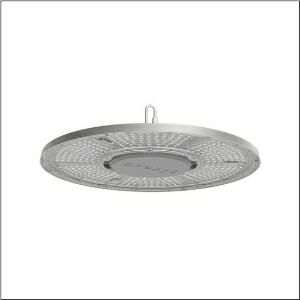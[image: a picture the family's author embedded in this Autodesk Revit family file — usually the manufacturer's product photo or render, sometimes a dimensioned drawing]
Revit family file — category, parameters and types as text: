
# Revit family: highbay_31-l_51hc42da4jmb
name_source: partatom
category: Lighting Fixtures
units: mm (PartAtom-declared; Revit-internal decimal feet)

## family parameters
Cut with Voids When Loaded = No
Host = Face
Light Source = No
Part Type = Normal
Room Calculation Point = No
Round Connector Dimension = Use Diameter
Shared = No

## types (1)
- Highbay 31-L (1 x LED, 20000 lm, 134 W, 4000K)
    Apparent Load = 134 VA
    CIE Flux Codes = 77 99 100 100 100
    Color Rendering = 80
    Color Temperature = 4000K
    Default Elevation = 1800 mm
    Description = Highbay 31-L, high bay luminaire, primary light control with lens, of PC, primary optical cover: cover panel, of PC, transparent, light emission: direct distribution, primary light characteristic: rotationally symmetric, installation type: suspended mounting, surface-mounted, LED, rated luminous flux: 20.000lm, luminous efficacy: 150lm/W, light colour: 840, colour temperature: 4000K, control gear: DALI 2, with cable, 5x 1.0mm², free wire ends, mains connection: 220..240V, AC/DC, 0/50..60Hz, cable length: 1,5m, rated input power: 134W, housing, rotationally symmetric, of diecast aluminium, powder-coated, grey aluminium (RAL 9007), with hook on luminaire side, incl. screw, diameter: 404mm, protection rating (complete): IP65, insulation class (complete): insulation class I (protective earthing), certification: CE, ENEC, UKCA, protection symbol: D, impact resistance: IK08, permissible operating ambient temperature: -30..+45°C, standard: EN 60598-2-22, EN 60598, corresponds to IFS (International Featured Standards) requirements for safety and quality in the food industry, packaging unit: 1 piece
    Height = 141 mm
    Lamp = 1 x LED
    Lamp Light Flux = 20000 lm
    Lamp Power = 134 W
    Lamp count = 1
    Length = 406 mm
    Luminous efficacy = 149 lm/W
    Manufacturer = Siteco
    ModVariant = No
    Model = 51HC42DA4JMB
    Mounting Place = Ceiling
    Mounting Type = Pendant
    Number of Poles = 1
    OnlyDefault = Yes
    Power Factor = 1
    Product Name = Highbay 31-L
    Product group = high bay luminaire
    ProductGroupID = 901
    Protection Class = Protection class I
    Protection Degree = IP 65
    RLX_Detail_Level = 1
    RLX_Emergency_Light_Flux = 0 lm
    RLX_Emergency_Type = 0
    RLX_Emergency_Type_DB = No
    RlxData = <blob elided: 172805 chars, md5=1e797721>
    Socket = socket
    Standby Power = 0 W
    System Light Flux = 20000 lm
    System Power = 134 W
    Type Comments = Product without accessories
    Type Image = l_1003610.jpg
    URL = http://relux.com
    VarID = ---
    Voltage = 0 V
    Weight = 0.00 kg
    Width = 0 mm  [stored 0 ft]

note: [stored X ft] marks values corroborated as IEEE doubles in the binary element streams (Revit-internal decimal feet)

## geometry (parser evidence)
native form markers: Blend x4, Sweep x8
no freeform markers — native parametric forms only
